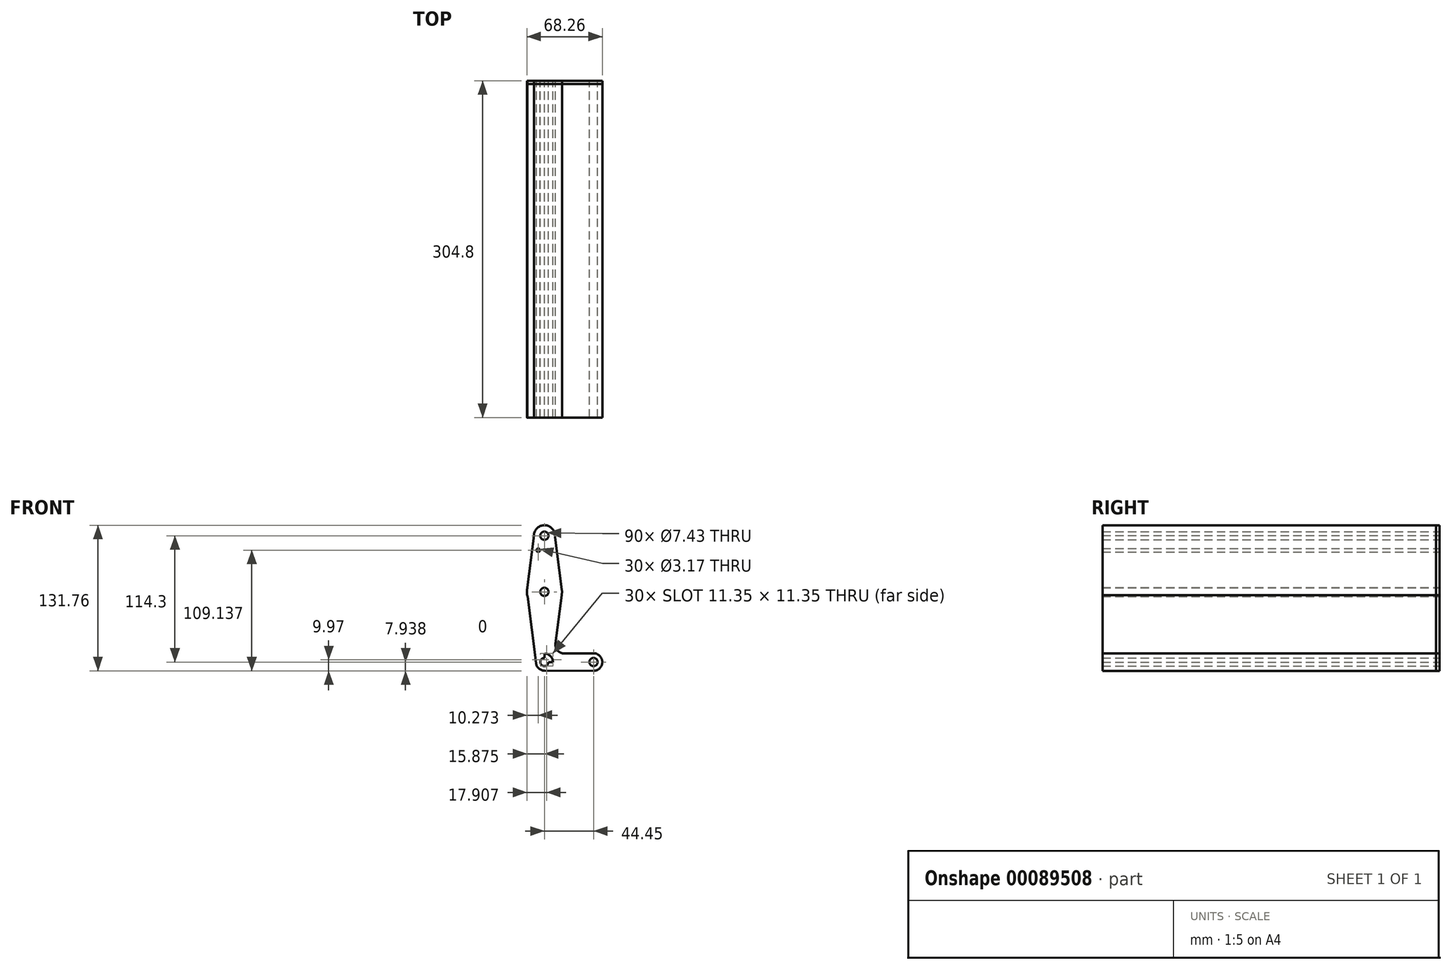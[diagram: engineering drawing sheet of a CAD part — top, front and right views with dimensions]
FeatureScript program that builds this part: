
annotation { "Feature Type Name" : "Feature", "Feature Type Description" : "" }
export const myFeature = defineFeature(function(context is Context, id is Id, definition is map)
    precondition{}
    {
        {
            var Q0;
            Q0=qCreatedBy(makeId("Front.planeOp"),FACE);
            var sketch = newSketch(context, id + "F0", { "sketchPlane" : qUnion([Q0])});
            skLineSegment(sketch, "E0", {"start": v(0.02, 114.4) * mm, "end": v(0.02, 0.1) * mm});
            skLineSegment(sketch, "E1", {"start": v(0.02, 0.1) * mm, "end": v(44.47, 0.1) * mm});
            skCircle(sketch, "E2", {"center": v(0.02, 114.4) * mm, "radius": 9.53 * mm});
            skCircle(sketch, "E3", {"center": v(0.02, 63.6) * mm, "radius": 15.88 * mm});
            skCircle(sketch, "E4", {"center": v(0.02, 0.1) * mm, "radius": 7.7 * mm});
            skCircle(sketch, "E5", {"center": v(44.47, 0.1) * mm, "radius": 7.94 * mm});
            skLineSegment(sketch, "E6", {"start": v(-9.5, 114.55) * mm, "end": v(-15.86, 63.35) * mm});
            skLineSegment(sketch, "E7", {"start": v(9.45, 115.67) * mm, "end": v(16.05, 63.35) * mm});
            skLineSegment(sketch, "E8", {"start": v(15.63, 60.75) * mm, "end": v(9.96, 16.87) * mm});
            skLineSegment(sketch, "E9", {"start": v(17.88, 7.9) * mm, "end": v(44.42, 8.04) * mm});
            skLineSegment(sketch, "E10", {"start": v(0, -7.6) * mm, "end": v(44.42, -7.84) * mm});
            skCircle(sketch, "E11", {"center": v(0.02, 114.4) * mm, "radius": 3.72 * mm});
            skCircle(sketch, "E12", {"center": v(0.02, 63.6) * mm, "radius": 3.72 * mm});
            skCircle(sketch, "E13", {"center": v(0.02, 0.1) * mm, "radius": 3.72 * mm});
            skCircle(sketch, "E14", {"center": v(44.47, 0.1) * mm, "radius": 3.72 * mm});
            skLineSegment(sketch, "E15", {"start": v(-15.27, 59.32) * mm, "end": v(-7.63, -0.87) * mm});
            skArc(sketch, "E16.filletArc", {"start": v(9.96, 16.87) * mm, "mid": v(11.88, 10.58) * mm, "end": v(17.88, 7.9) * mm});
            skCircle(sketch, "E17", {"center": v(-5.59, 101.3) * mm, "radius": 1.59 * mm});
            skSolve(sketch);
        }
        {
            var Q0;
            Q0 = qSketchRegion(id + "F0", true);
            extrude(context, id + "F1", {"entities" : qUnion([Q0]), "depth" : 304.8 * mm});
        }
        {
            var Q0;
            Q0 = qSketchRegion(id + "F0", true);
            extrude(context, id + "F2", {"entities" : qUnion([Q0]), "depth" : 3.05 * mm});
        }
    });
